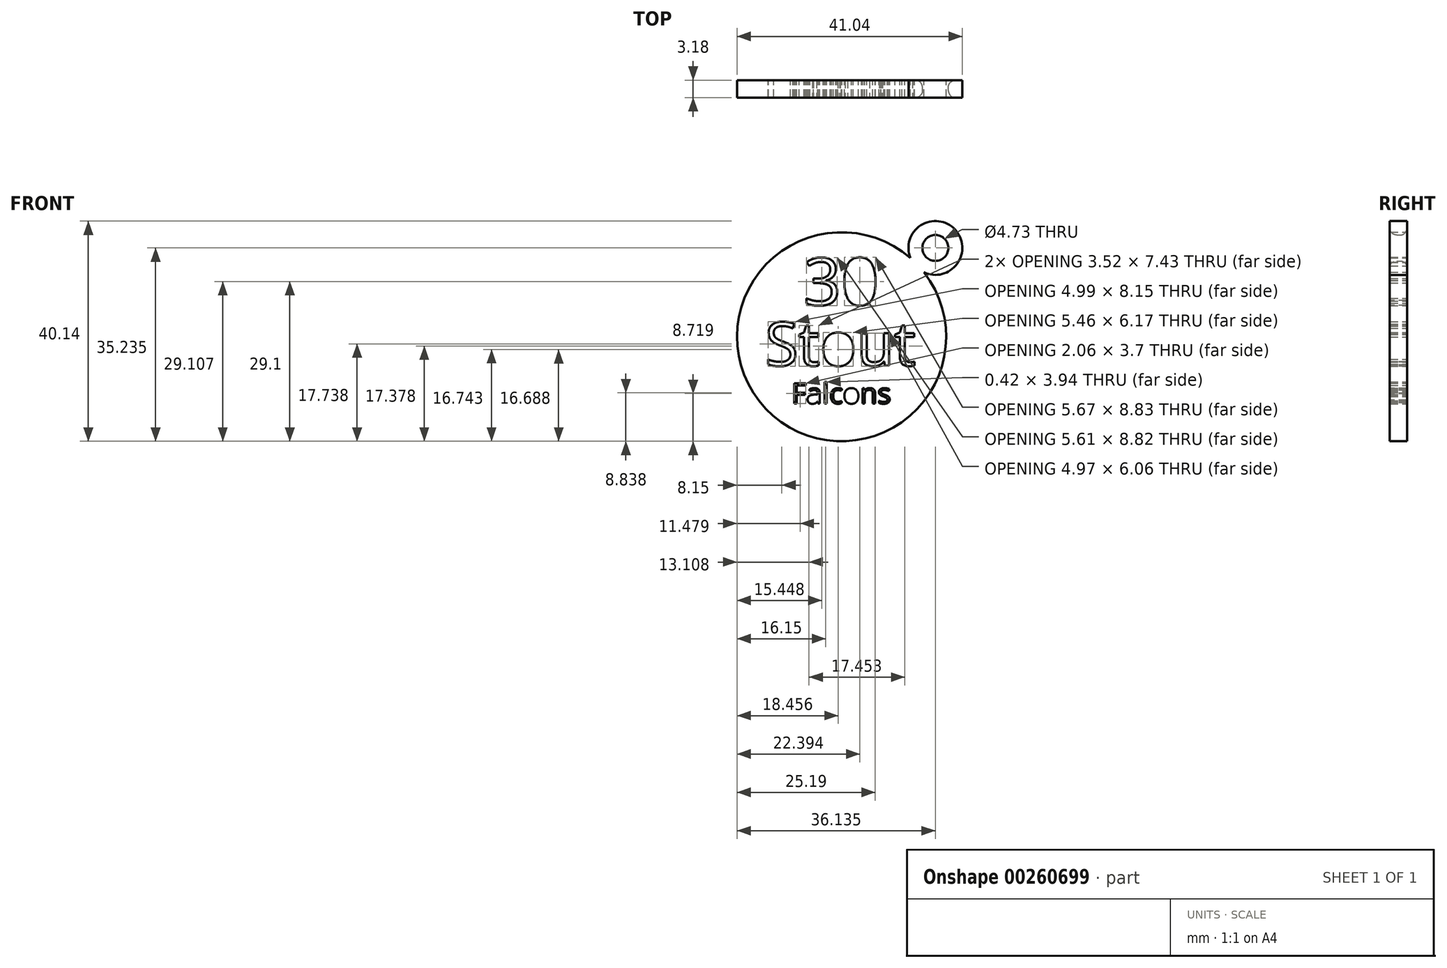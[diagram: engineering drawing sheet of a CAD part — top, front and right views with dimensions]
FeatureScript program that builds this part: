
annotation { "Feature Type Name" : "Feature", "Feature Type Description" : "" }
export const myFeature = defineFeature(function(context is Context, id is Id, definition is map)
    precondition{}
    {
        {
            var Q0;
            Q0=qCreatedBy(makeId("Front.planeOp"),FACE);
            var sketch = newSketch(context, id + "F0", { "sketchPlane" : qUnion([Q0])});
            skCircle(sketch, "E0", {"center": v(0, 0) * mm, "radius": 19.05 * mm});
            skText(sketch, "E1", { "text": "Stout", "fontName": "OpenSans-Regular.ttf"});
            skText(sketch, "E2", { "text": "30", "fontName": "OpenSans-Regular.ttf"});
            skText(sketch, "E3", { "text": "Falcons", "fontName": "OpenSans-Regular.ttf"});
            const initialGuessF0  = {"E1": [-0.01397, -0.00528, 1, 0, 0.008], "E2": [-0.00696, 0.00576, 1, 0, 0.00865], "E3": [-0.00911, -0.01218, 1, 0, 0.00373]};
            skSetInitialGuess(sketch, initialGuessF0);
            skSolve(sketch);
        }
        {
            var Q0;
            Q0=makeQuery(id+"F0.imprint","IMPRINT",FACE,{"disambiguationData":[TD([[makeQuery(id+"F0.imprint","IMPRINT",EDGE,{"derivedFrom":sQuery(id+"F0.wireOp",EDGE,"E0")}),1.0]])]});
            extrude(context, id + "F1", {"entities" : qUnion([Q0]), "depth" : 3.17 * mm});
        }
        {
            var Q0;
            Q0=qCreatedBy(makeId("Front.planeOp"),FACE);
            var sketch = newSketch(context, id + "F2", { "sketchPlane" : qUnion([Q0])});
            skCircle(sketch, "E4", {"center": v(17.08, 16.19) * mm, "radius": 4.9 * mm});
            skPoint(sketch, "E4.first.point", {"position": v(13.24, 13.14) * mm});
            skPoint(sketch, "E4.second.point", {"position": v(21.02, 13.25) * mm});
            skPoint(sketch, "E4.third.point", {"position": v(13, 18.91) * mm});
            skCircle(sketch, "E5", {"center": v(17.08, 16.19) * mm, "radius": 2.37 * mm});
            skSolve(sketch);
        }
        {
            var Q0;
            Q0=makeQuery(id+"F2.imprint","IMPRINT",FACE,{"disambiguationData":[TD([[makeQuery(id+"F2.imprint","IMPRINT",EDGE,{"derivedFrom":sQuery(id+"F2.wireOp",EDGE,"E4")}),1.0]])]});
            extrude(context, id + "F3", {"entities" : qUnion([Q0]), "operationType" : NewBodyOperationType.ADD, "depth" : 3.17 * mm});
        }
        {
            var Q0;
            Q0=makeQuery(id+"F3.opExtrude","CAP_EDGE",EDGE,{"disambiguationData":[OSD([sQuery(id+"F2.wireOp",EDGE,"E5")])],"isStart":false});
            fillet(context, id + "F4", {"entities" : qUnion([Q0]), "radius" : 1.27 * mm, "tangentPropagation" : true, "allowEdgeOverflow" : false});
        }
        {
            var Q0;
            Q0=makeQuery(id+"F3.opExtrude","CAP_EDGE",EDGE,{"disambiguationData":[OSD([sQuery(id+"F2.wireOp",EDGE,"E5")])],"isStart":true});
            fillet(context, id + "F5", {"entities" : qUnion([Q0]), "radius" : 1.27 * mm, "tangentPropagation" : true, "allowEdgeOverflow" : false});
        }
    });
